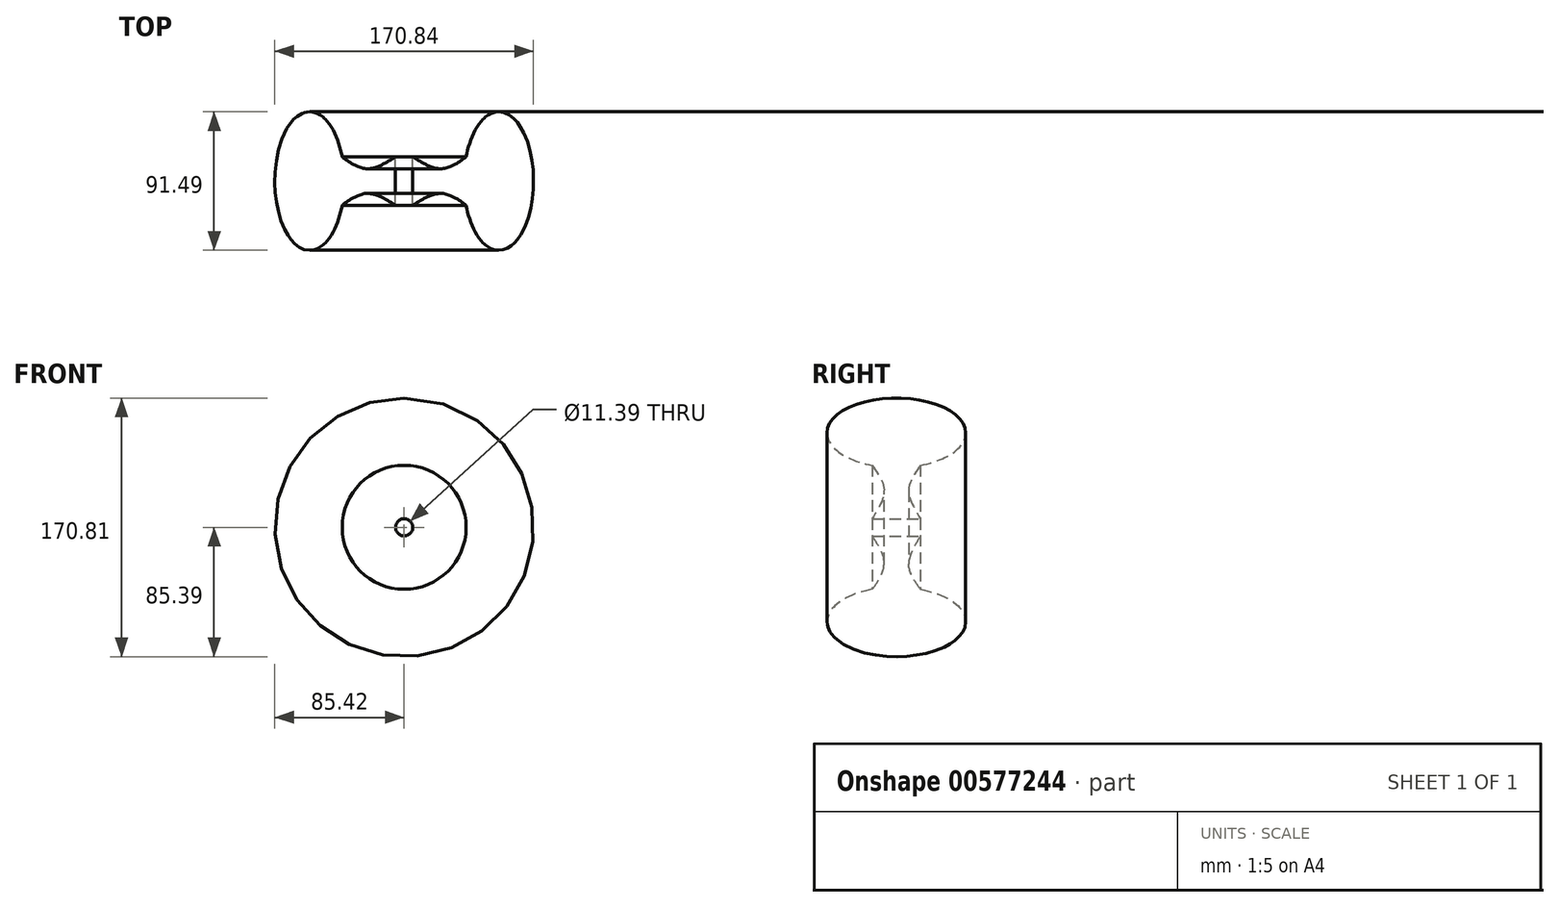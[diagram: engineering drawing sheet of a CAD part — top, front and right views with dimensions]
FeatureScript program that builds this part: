
annotation { "Feature Type Name" : "Feature", "Feature Type Description" : "" }
export const myFeature = defineFeature(function(context is Context, id is Id, definition is map)
    precondition{}
    {
        {
            var Q0;
            Q0=qCreatedBy(makeId("Top.planeOp"),FACE);
            var sketch = newSketch(context, id + "F0", { "sketchPlane" : qUnion([Q0])});
            skEllipticalArc(sketch, "E0", {});
            skFitSpline(sketch, "E1", {"points": [v(-40.92, 23.25) * mm, v(-24.49, 15.47) * mm, v(-5.7, 23.25) * mm], "startDerivative": vector(33.2, -23.56) * mm, "endDerivative": vector(37.27, 23.15) * mm});
            skFitSpline(sketch, "E2.MirrorCS", {"points": [v(-40.92, -8.63) * mm, v(-24.49, -0.85) * mm, v(-5.7, -8.64) * mm], "startDerivative": vector(33.2, 23.56) * mm, "endDerivative": vector(37.27, -23.15) * mm});
            skLineSegment(sketch, "E3", {"start": v(-5.7, 23.25) * mm, "end": v(-5.7, -8.64) * mm});
            skLineSegment(sketch, "E4", {"start": v(0, 27.47) * mm, "end": v(0, -26.28) * mm});
            const initialGuessF0  = {"E0": [-0.06245145946741104, 0.0073081497102975845, 0, -1, 0.045747118070721626, 0.022971635350291834, 1.9267582385531337, 1.2148344150366592]};
            skSetInitialGuess(sketch, initialGuessF0);
            skSolve(sketch);
        }
        {
            var Q0;
            Q0=makeQuery(id+"F0.imprint","IMPRINT",FACE,{"disambiguationData":[TD([[makeQuery(id+"F0.imprint","IMPRINT",EDGE,{"derivedFrom":sQuery(id+"F0.wireOp",EDGE,"E0")}),1.0]])]});
            var Q1;
            Q1=sQuery(id+"F0.wireOp",EDGE,"E4");
            revolve(context, id + "F1", {"entities" : qUnion([Q0]), "axis" : qUnion([Q1]), "revolveType" : RevolveType.FULL});
        }
    });
